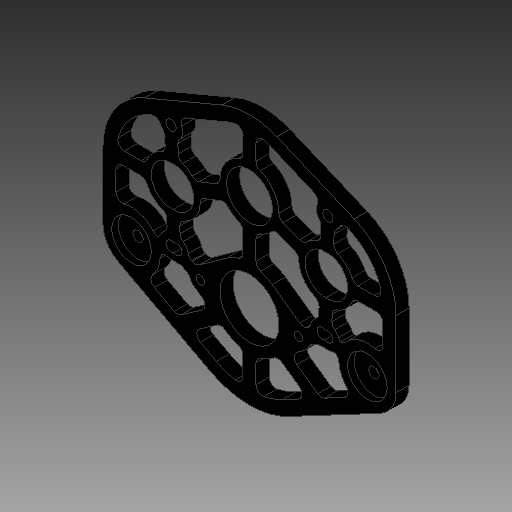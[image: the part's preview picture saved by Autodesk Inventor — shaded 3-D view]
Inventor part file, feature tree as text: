
AUTODESK INVENTOR PART (.ipt)
format: ipt  version: 2019 (Build 230136000, 136)  size: 401,920 bytes
history: native  units: in
note: dims shown in document units (in); Inventor stores cm internally (conversion verified against a paired STEP export)
features: mirror x1
ambient origin geometry x8: Origin, YZ Plane, XZ Plane, XY Plane, X Axis, Y Axis, Z Axis, Center Point
bodies: Solid1 (feature_tree)
feature tree (1):
  mirror  "Mirror1"
